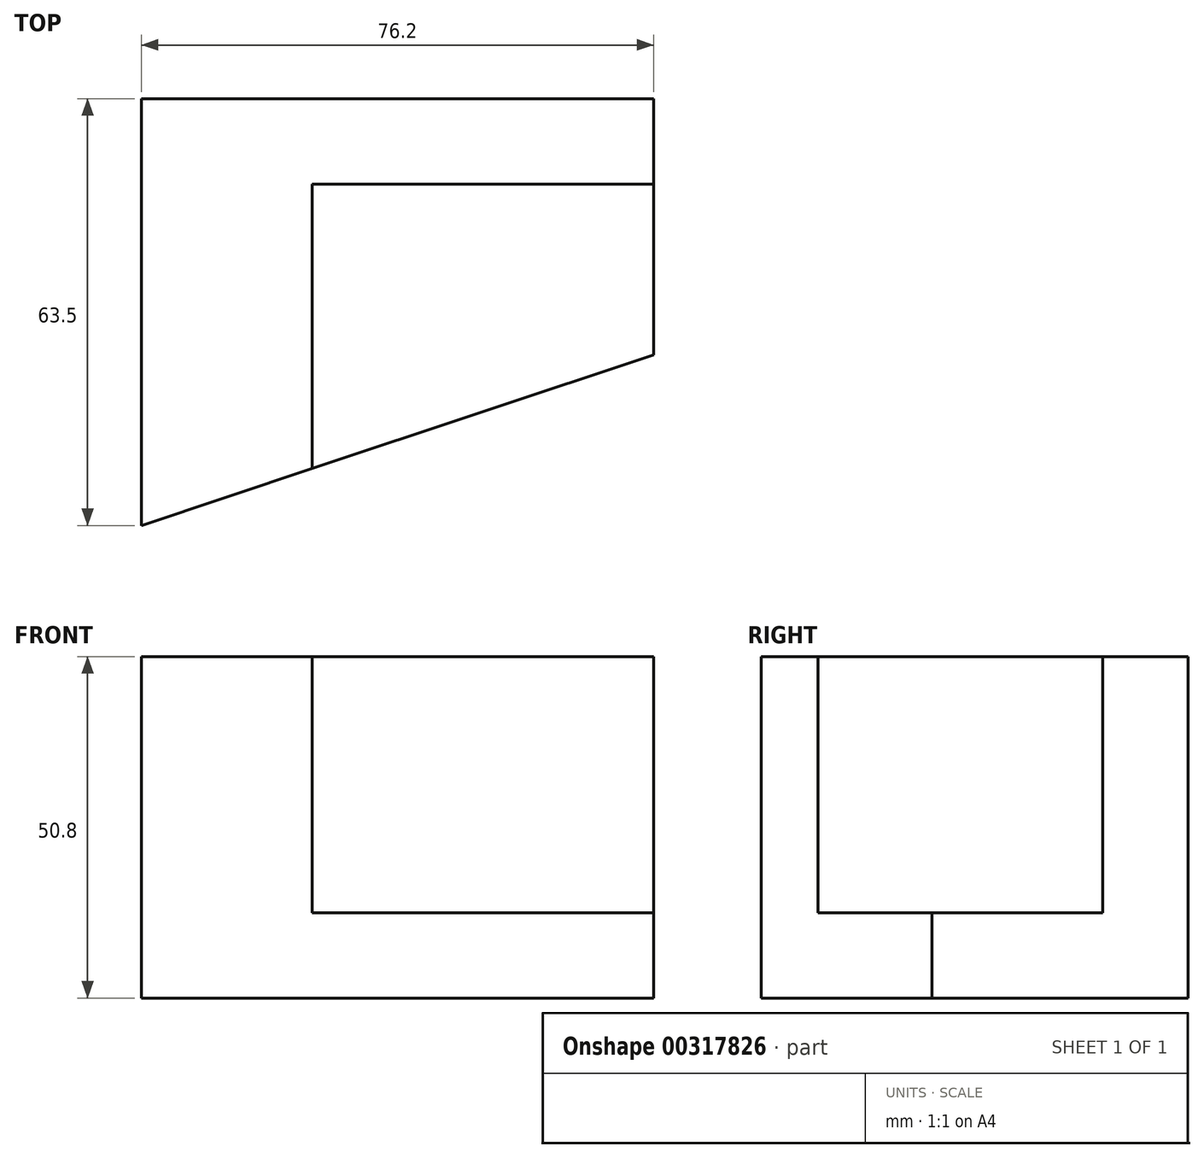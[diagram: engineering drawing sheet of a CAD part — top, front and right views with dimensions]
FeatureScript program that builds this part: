
annotation { "Feature Type Name" : "Feature", "Feature Type Description" : "" }
export const myFeature = defineFeature(function(context is Context, id is Id, definition is map)
    precondition{}
    {
        {
            var Q0;
            Q0=qCreatedBy(makeId("Front.planeOp"),FACE);
            var sketch = newSketch(context, id + "F0", { "sketchPlane" : qUnion([Q0])});
            skLineSegment(sketch, "E0", {"start": v(0, 0) * mm, "end": v(0, 50.8) * mm});
            skLineSegment(sketch, "E1", {"start": v(0, 50.8) * mm, "end": v(76.2, 50.8) * mm});
            skLineSegment(sketch, "E2", {"start": v(76.2, 50.8) * mm, "end": v(76.2, 0) * mm});
            skLineSegment(sketch, "E3", {"start": v(76.2, 0) * mm, "end": v(0, 0) * mm});
            skSolve(sketch);
        }
        {
            var Q0;
            Q0 = qSketchRegion(id + "F0", true);
            extrude(context, id + "F1", {"entities" : qUnion([Q0]), "depth" : 63.5 * mm});
        }
        {
            var Q0;
            Q0=makeQuery(id+"F1.opExtrude","CAP_FACE",FACE,{"disambiguationData":[OSD([sQuery(id+"F0.wireOp",EDGE,"E0"),sQuery(id+"F0.wireOp",EDGE,"E1"),sQuery(id+"F0.wireOp",EDGE,"E2"),sQuery(id+"F0.wireOp",EDGE,"E3")])],"isStart":false});
            var sketch = newSketch(context, id + "F2", { "sketchPlane" : qUnion([Q0])});
            skLineSegment(sketch, "E4", {"start": v(0, 50.8) * mm, "end": v(0, 0) * mm});
            skLineSegment(sketch, "E5", {"start": v(0, 0) * mm, "end": v(76.2, 0) * mm});
            skLineSegment(sketch, "E6", {"start": v(76.2, 0) * mm, "end": v(76.2, 12.7) * mm});
            skLineSegment(sketch, "E7", {"start": v(76.2, 12.7) * mm, "end": v(25.4, 12.7) * mm});
            skLineSegment(sketch, "E8", {"start": v(25.4, 12.7) * mm, "end": v(25.4, 50.8) * mm});
            skLineSegment(sketch, "E9", {"start": v(25.4, 50.8) * mm, "end": v(0, 50.8) * mm});
            skSolve(sketch);
        }
        {
            var Q0;
            {var subQ0=sQuery(id+"F2.wireOp",EDGE,"E7");Q0=makeQuery(id+"F2.imprint","IMPRINT",FACE,{"disambiguationData":[TD([[makeQuery(id+"F2.imprint","IMPRINT",EDGE,{"derivedFrom":subQ0}),-1.0]])]});}
            extrude(context, id + "F3", {"entities" : qUnion([Q0]), "operationType" : NewBodyOperationType.REMOVE, "oppositeDirection" : true, "depth" : 50.8 * mm});
        }
        {
            var Q0;
            Q0=makeQuery(id+"F1.opExtrude","SWEPT_FACE",FACE,{"disambiguationData":[OSD([sQuery(id+"F0.wireOp",EDGE,"E3")])]});
            var sketch = newSketch(context, id + "F4", { "sketchPlane" : qUnion([Q0])});
            skLineSegment(sketch, "E10", {"start": v(0, 63.5) * mm, "end": v(0, 0) * mm});
            skLineSegment(sketch, "E11", {"start": v(0, 0) * mm, "end": v(76.2, 0) * mm});
            skLineSegment(sketch, "E12", {"start": v(76.2, 0) * mm, "end": v(76.2, 38.1) * mm});
            skLineSegment(sketch, "E13", {"start": v(76.2, 38.1) * mm, "end": v(0, 63.5) * mm});
            skSolve(sketch);
        }
        {
            var Q0;
            {var subQ0=sQuery(id+"F4.wireOp",EDGE,"E13");Q0=makeQuery(id+"F4.imprint","IMPRINT",FACE,{"disambiguationData":[TD([[makeQuery(id+"F4.imprint","IMPRINT",EDGE,{"derivedFrom":subQ0}),-1.0]])]});}
            extrude(context, id + "F5", {"entities" : qUnion([Q0]), "operationType" : NewBodyOperationType.REMOVE, "endBound" : BoundingType.THROUGH_ALL, "oppositeDirection" : true, "depth" : 25.4 * mm});
        }
    });
